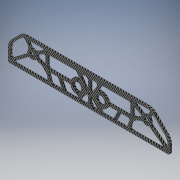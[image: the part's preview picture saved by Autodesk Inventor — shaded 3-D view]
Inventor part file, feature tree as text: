
AUTODESK INVENTOR PART (.ipt)
format: ipt  version: 2018.3 (Build 223284000, 284)  size: 885,760 bytes
history: native  units: mm
features: extrude x16, sketch x15, fillet x11, projected_geometry x3
ambient origin geometry x8: Origin, YZ Plane, XZ Plane, XY Plane, X Axis, Y Axis, Z Axis, Center Point
bodies: Solid1 (feature_tree), Body1 (feature_tree)
feature tree (45):
  extrude  "Extrusion1"  Depth=22.5mm
  extrude  "Extrusion2"  Depth=10.0mm
  extrude  "Extrusion3"  Depth=7.5mm
  fillet  "Fillet1"  Radius=7.5mm
  extrude  "Extrusion4"  Depth=10.0mm TaperAngle=0.0deg
  extrude  "Extrusion5"  Depth=5.0mm
  extrude  "Extrusion6"  Depth=7.5mm
  extrude  "Extrusion7"  Depth=7.5mm
  sketch  "Sketch11"  dims[d19=7.5mm d20=5.0mm d21=0.0mm]
  extrude  "Extrusion8"  Depth=5.0mm TaperAngle=0.0deg
  extrude  "Extrusion9"  Depth=7.5mm
  extrude  "Extrusion10"  Depth=6.0mm
  extrude  "Extrusion11"  Depth=3.0mm
  extrude  "Extrusion12"  Depth=10.0mm TaperAngle=0.0deg
  extrude  "Extrusion13"  Depth=10.0mm TaperAngle=0.0deg
  extrude  "Extrusion14"  Depth=10.0mm TaperAngle=0.0deg
  extrude  "Extrusion15"  Depth=10.0mm
  fillet  "Fillet2"  Radius=10.0mm
  fillet  "Fillet3"  Radius=3.0mm
  fillet  "Fillet4"  Radius=3.0mm
  fillet  "Fillet5"  Radius=10.0mm
  fillet  "Fillet6"  Radius=10.0mm
  fillet  "Fillet7"  Radius=6.0mm
  fillet  "Fillet8"  Radius=3.0mm
  fillet  "Fillet9"  Radius=3.0mm
  fillet  "Fillet10"  Radius=3.0mm
  fillet  "Fillet11"  Radius=3.0mm
  extrude  "Extrusion16"  Depth=3.0mm
  sketch  "Sketch1"  dims[d0=22.5mm d1=22.5mm]
  sketch  "Sketch2"  dims[d2=10.0mm d3=0.0mm d4=34.677mm]
  sketch  "Sketch3"  dims[d6=10.0mm d7=0.0mm d8=3.1mm d9=7.5mm]
  sketch  "Sketch4"  dims[d10=10.0mm d11=10.0mm d12=0.0mm]
  projected_geometry  "Projected Loop1"
  sketch  "Sketch5"  dims[d13=5.0mm d14=3.1mm]
  projected_geometry  "Projected Loop2"
  sketch  "Sketch8"  dims[d15=7.5mm d16=7.5mm]
  projected_geometry  "Projected Loop3"
  sketch  "Sketch9"  dims[d17=3.1mm d18=7.5mm]
  sketch  "Sketch12"  dims[d22=5.0mm d23=0.0mm d24=7.5mm]
  sketch  "Sketch13"  dims[d25=6.0mm d26=6.0mm d27=6.0mm d28=6.0mm d29=8.0mm d30=8.0mm d31=6.0mm d32=6.0mm d33=6.0mm d34=6.0mm d35=6.0mm d36=6.0mm d37=6.0mm d38=6.0mm d69=18.915mm]
  sketch  "Sketch14"  dims[d72=3.0mm d73=3.0mm]
  sketch  "Sketch15"  dims[d74=10.0mm d75=0.0mm d78=10.0mm d79=0.0mm]
  sketch  "Sketch16"  dims[d91=10.0mm d92=0.0mm d93=10.0mm d94=0.0mm]
  sketch  "Sketch17"  dims[d95=10.0mm d96=0.0mm d98=10.0mm d99=0.0mm]
  sketch  "Sketch18"  dims[d100=10.0mm d101=0.0mm d106=15.0mm d107=10.0mm d108=0.0mm d109=3.0mm d110=3.0mm d111=10.0mm d112=0.0mm d113=10.0mm d114=0.0mm d115=6.0mm d116=3.0mm d117=3.0mm d118=3.0mm d119=3.0mm d120=3.0mm d121=3.0mm d122=6.0mm d123=3.0mm d124=3.0mm d128=3.0mm d129=10.0mm d130=0.0mm]
